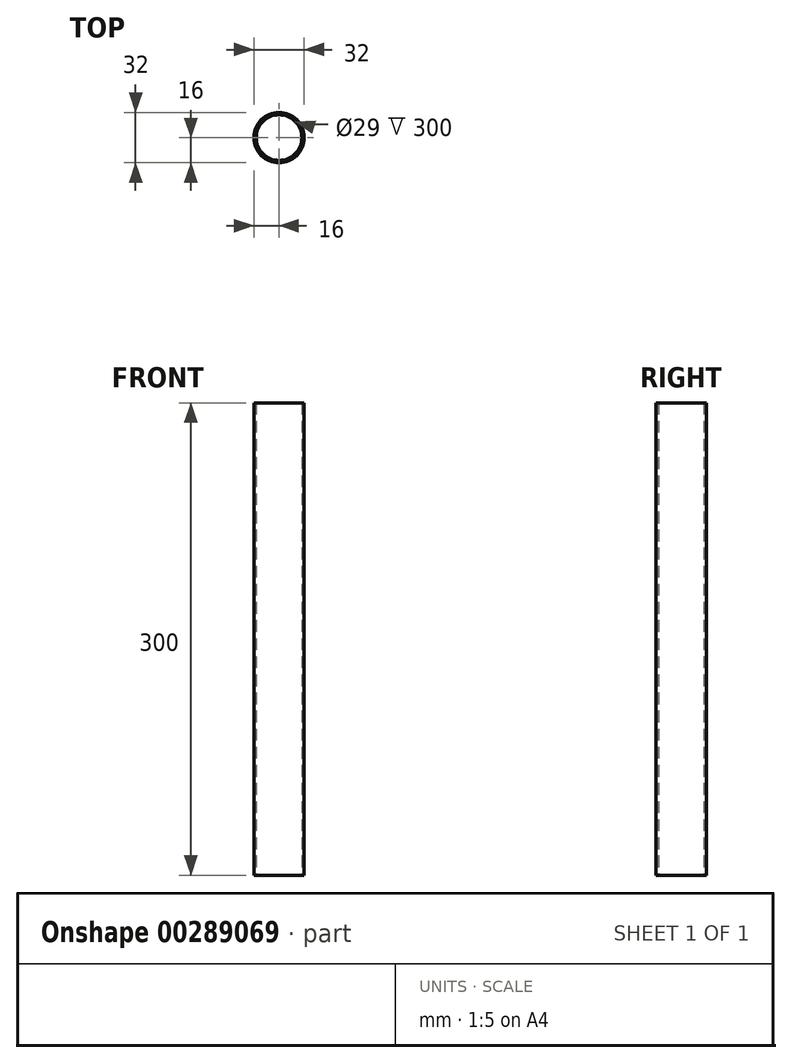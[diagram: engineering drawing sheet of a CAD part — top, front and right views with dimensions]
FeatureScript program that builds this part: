
annotation { "Feature Type Name" : "Feature", "Feature Type Description" : "" }
export const myFeature = defineFeature(function(context is Context, id is Id, definition is map)
    precondition{}
    {
        {
            var Q0;
            Q0=qCreatedBy(makeId("Top.planeOp"),FACE);
            var sketch = newSketch(context, id + "F0", { "sketchPlane" : qUnion([Q0])});
            skCircle(sketch, "E0", {"center": v(0, 0) * mm, "radius": 14.5 * mm});
            skCircle(sketch, "E1", {"center": v(0, 0) * mm, "radius": 16 * mm});
            skSolve(sketch);
        }
        {
            var Q0;
            Q0=makeQuery(id+"F0.imprint","IMPRINT",FACE,{"disambiguationData":[TD([[makeQuery(id+"F0.imprint","IMPRINT",EDGE,{"derivedFrom":sQuery(id+"F0.wireOp",EDGE,"E0")}),-1.0]])]});
            extrude(context, id + "F1", {"entities" : qUnion([Q0]), "depth" : 300 * mm});
        }
    });
